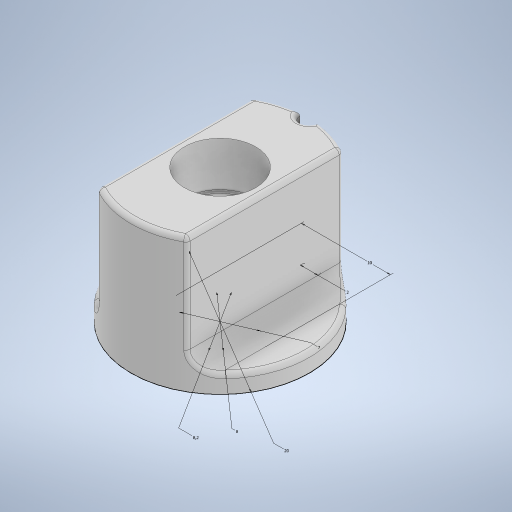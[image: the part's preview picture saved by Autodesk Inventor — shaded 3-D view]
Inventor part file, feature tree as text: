
AUTODESK INVENTOR PART (.ipt)
format: ipt  version: 2024 (Build 280153000, 153)  size: 390,656 bytes
history: native  units: mm
features: extrude x7, fillet x4, sketch x2, other x1
ambient origin geometry x8: Origin, YZ Plane, XZ Plane, XY Plane, X Axis, Y Axis, Z Axis, Center Point
bodies: Body1 (feature_tree)
feature tree (14):
  other  "Твердое тело1"
  sketch  "Эскиз1"
  extrude  "Выдавливание1"  Depth=6.15mm
  extrude  "Выдавливание2"  Depth=8.0mm
  fillet  "Сопряжение3"  Radius=20.0mm
  fillet  "Сопряжение7"  Radius=10.0mm
  fillet  "Сопряжение8"  Radius=2.0mm
  extrude  "Выдавливание7"  Depth=2.0mm TaperAngle=0.0deg
  extrude  "Выдавливание8"  Depth=15.0mm TaperAngle=0.0deg
  fillet  "Сопряжение12"  Radius=2.0mm
  extrude  "Выдавливание10"  Depth=7.0mm
  extrude  "Выдавливание11"  Depth=0.5mm
  extrude  "Выдавливание12"  Depth=0.5mm
  sketch  "Эскиз4"
